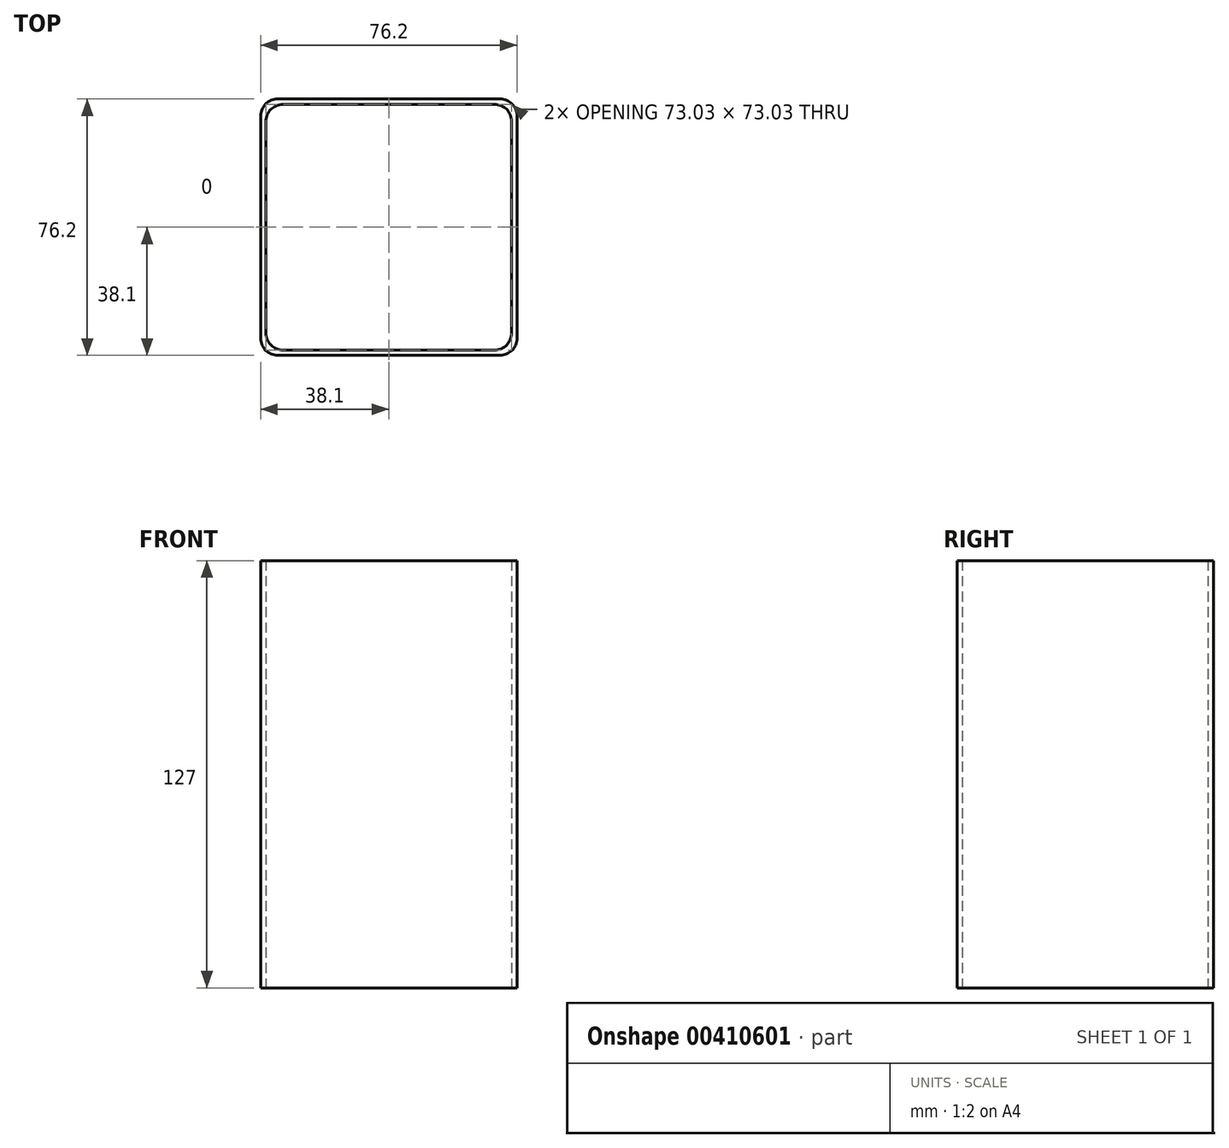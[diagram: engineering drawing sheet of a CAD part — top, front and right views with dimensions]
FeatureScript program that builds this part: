
annotation { "Feature Type Name" : "Feature", "Feature Type Description" : "" }
export const myFeature = defineFeature(function(context is Context, id is Id, definition is map)
    precondition{}
    {
        {
            var Q0;
            Q0=qCreatedBy(makeId("Top.planeOp"),FACE);
            var sketch = newSketch(context, id + "F0", { "sketchPlane" : qUnion([Q0])});
            skLineSegment(sketch, "E0.bottom", {"start": v(-38.1, -38.1) * mm, "end": v(38.1, -38.1) * mm});
            skLineSegment(sketch, "E0.top", {"start": v(-38.1, 38.1) * mm, "end": v(38.1, 38.1) * mm});
            skLineSegment(sketch, "E0.left", {"start": v(-38.1, -38.1) * mm, "end": v(-38.1, 38.1) * mm});
            skLineSegment(sketch, "E0.right", {"start": v(38.1, -38.1) * mm, "end": v(38.1, 38.1) * mm});
            skPoint(sketch, "E0.middle", {"position": v(0, 0) * mm});
            skLineSegment(sketch, "E1.bottom", {"start": v(-36.51, -36.51) * mm, "end": v(36.51, -36.51) * mm});
            skLineSegment(sketch, "E1.top", {"start": v(-36.51, 36.51) * mm, "end": v(36.51, 36.51) * mm});
            skLineSegment(sketch, "E1.left", {"start": v(-36.51, -36.51) * mm, "end": v(-36.51, 36.51) * mm});
            skLineSegment(sketch, "E1.right", {"start": v(36.51, -36.51) * mm, "end": v(36.51, 36.51) * mm});
            skSolve(sketch);
        }
        {
            var Q0;
            Q0=makeQuery(id+"F0.imprint","IMPRINT",FACE,{"disambiguationData":[TD([[makeQuery(id+"F0.imprint","IMPRINT",EDGE,{"derivedFrom":sQuery(id+"F0.wireOp",EDGE,"E0.bottom")}),1.0]])]});
            extrude(context, id + "F1", {"entities" : qUnion([Q0]), "depth" : 127 * mm});
        }
        {
            var Q0;
            Q0=makeQuery(id+"F1.opExtrude","SWEPT_EDGE",EDGE,{"disambiguationData":[OSD([sQuery(id+"F0.wireOp",EDGE,"E1.top"),sQuery(id+"F0.wireOp",EDGE,"E1.left")])]});
            var Q1;
            Q1=makeQuery(id+"F1.opExtrude","SWEPT_EDGE",EDGE,{"disambiguationData":[OSD([sQuery(id+"F0.wireOp",EDGE,"E0.bottom"),sQuery(id+"F0.wireOp",EDGE,"E0.right")])]});
            var Q2;
            Q2=makeQuery(id+"F1.opExtrude","SWEPT_EDGE",EDGE,{"disambiguationData":[OSD([sQuery(id+"F0.wireOp",EDGE,"E0.bottom"),sQuery(id+"F0.wireOp",EDGE,"E0.left")])]});
            var Q3;
            Q3=makeQuery(id+"F1.opExtrude","SWEPT_EDGE",EDGE,{"disambiguationData":[OSD([sQuery(id+"F0.wireOp",EDGE,"E0.top"),sQuery(id+"F0.wireOp",EDGE,"E0.right")])]});
            var Q4;
            Q4=makeQuery(id+"F1.opExtrude","SWEPT_EDGE",EDGE,{"disambiguationData":[OSD([sQuery(id+"F0.wireOp",EDGE,"E1.top"),sQuery(id+"F0.wireOp",EDGE,"E1.right")])]});
            var Q5;
            Q5=makeQuery(id+"F1.opExtrude","SWEPT_EDGE",EDGE,{"disambiguationData":[OSD([sQuery(id+"F0.wireOp",EDGE,"E0.top"),sQuery(id+"F0.wireOp",EDGE,"E0.left")])]});
            var Q6;
            Q6=makeQuery(id+"F1.opExtrude","SWEPT_EDGE",EDGE,{"disambiguationData":[OSD([sQuery(id+"F0.wireOp",EDGE,"E1.bottom"),sQuery(id+"F0.wireOp",EDGE,"E1.right")])]});
            var Q7;
            Q7=makeQuery(id+"F1.opExtrude","SWEPT_EDGE",EDGE,{"disambiguationData":[OSD([sQuery(id+"F0.wireOp",EDGE,"E1.bottom"),sQuery(id+"F0.wireOp",EDGE,"E1.left")])]});
            fillet(context, id + "F2", {"entities" : qUnion([Q0, Q1, Q2, Q3, Q4, Q5, Q6, Q7]), "radius" : 5.08 * mm, "tangentPropagation" : true, "allowEdgeOverflow" : false});
        }
    });
